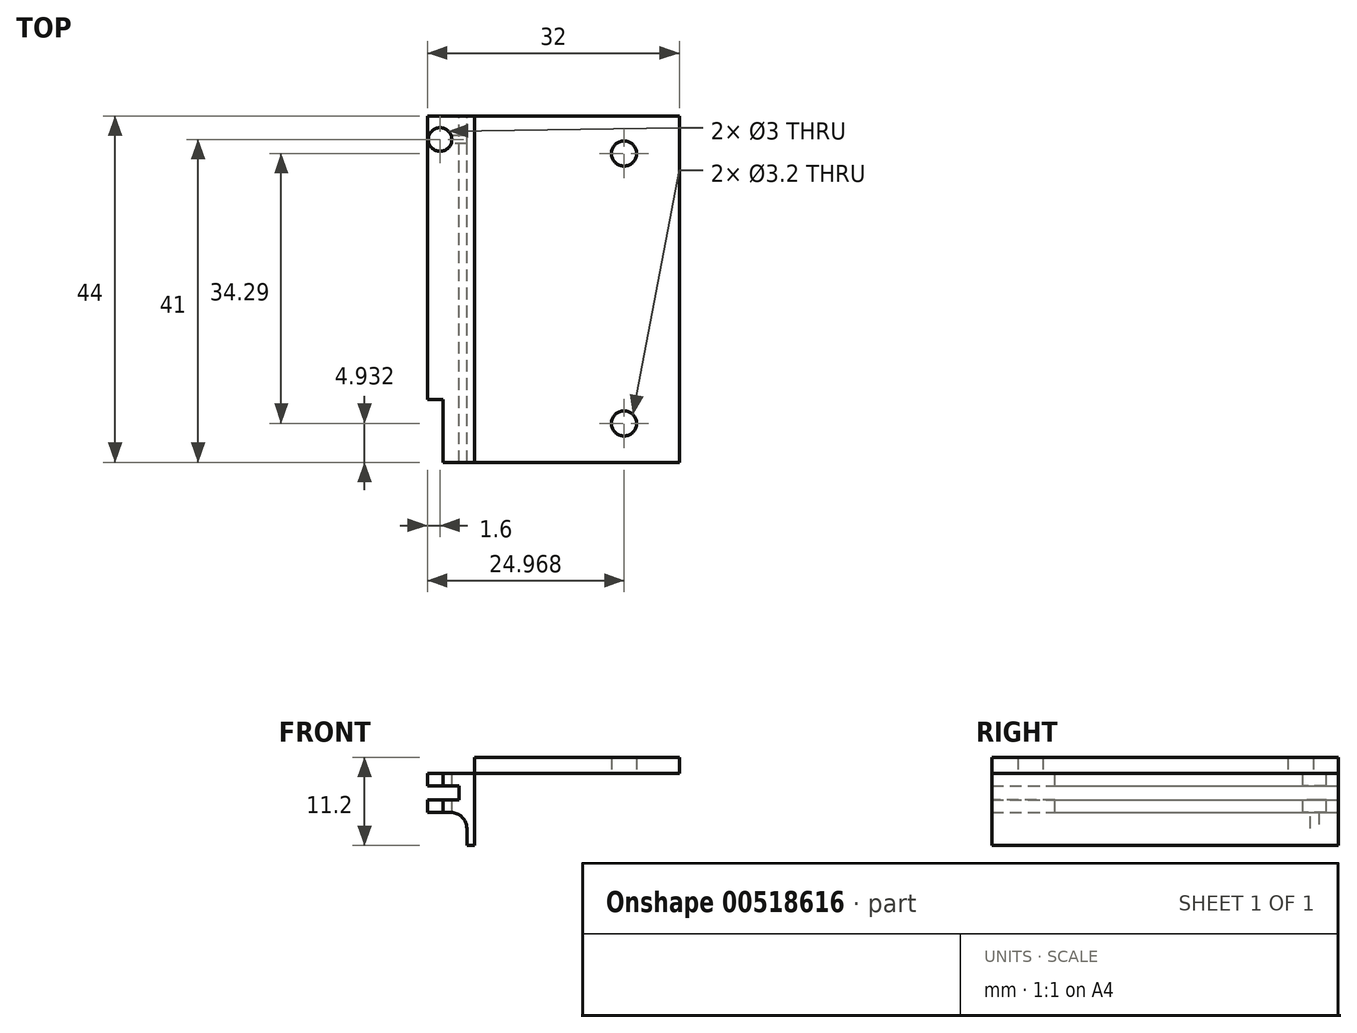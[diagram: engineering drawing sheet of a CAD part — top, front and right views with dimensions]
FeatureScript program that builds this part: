
annotation { "Feature Type Name" : "Feature", "Feature Type Description" : "" }
export const myFeature = defineFeature(function(context is Context, id is Id, definition is map)
    precondition{}
    {
        {
            var Q0;
            Q0=qCreatedBy(makeId("Front.planeOp"),FACE);
            var sketch = newSketch(context, id + "F0", { "sketchPlane" : qUnion([Q0])});
            skLineSegment(sketch, "E0", {"start": v(0, 0) * mm, "end": v(0, 9.2) * mm});
            skLineSegment(sketch, "E1", {"start": v(0, 9.2) * mm, "end": v(-6, 9.2) * mm});
            skLineSegment(sketch, "E2", {"start": v(-6, 9.2) * mm, "end": v(-6, 7.6) * mm});
            skLineSegment(sketch, "E3", {"start": v(-6, 7.6) * mm, "end": v(-2, 7.6) * mm});
            skLineSegment(sketch, "E4", {"start": v(-2, 7.6) * mm, "end": v(-2, 5.8) * mm});
            skLineSegment(sketch, "E5", {"start": v(-2, 5.8) * mm, "end": v(-6, 5.8) * mm});
            skLineSegment(sketch, "E6", {"start": v(-6, 5.8) * mm, "end": v(-6, 4.2) * mm});
            skLineSegment(sketch, "E7", {"start": v(-6, 4.2) * mm, "end": v(-1, 4.2) * mm});
            skLineSegment(sketch, "E8", {"start": v(-1, 4.2) * mm, "end": v(-1, 0) * mm});
            skLineSegment(sketch, "E9", {"start": v(-1, 0) * mm, "end": v(0, 0) * mm});
            skSolve(sketch);
        }
        {
            var Q0;
            Q0=makeQuery(id+"F0.imprint","IMPRINT",FACE,{"disambiguationData":[TD([[makeQuery(id+"F0.imprint","IMPRINT",EDGE,{"derivedFrom":sQuery(id+"F0.wireOp",EDGE,"E0")}),1.0]])]});
            extrude(context, id + "F1", {"entities" : qUnion([Q0]), "depth" : 44 * mm, "offsetDistance" : 25 * mm});
        }
        {
            var Q0;
            Q0=makeQuery(id+"F1.opExtrude","SWEPT_FACE",FACE,{"disambiguationData":[OSD([sQuery(id+"F0.wireOp",EDGE,"E1")])]});
            var sketch = newSketch(context, id + "F2", { "sketchPlane" : qUnion([Q0])});
            skCircle(sketch, "E10", {"center": v(-4.4, -3) * mm, "radius": 1.5 * mm});
            skSolve(sketch);
        }
        {
            var Q0;
            Q0=makeQuery(id+"F2.imprint","IMPRINT",FACE,{"disambiguationData":[TD([[makeQuery(id+"F2.imprint","IMPRINT",EDGE,{"derivedFrom":sQuery(id+"F2.wireOp",EDGE,"E10")}),1.0]])]});
            extrude(context, id + "F3", {"entities" : qUnion([Q0]), "operationType" : NewBodyOperationType.REMOVE, "endBound" : BoundingType.THROUGH_ALL, "oppositeDirection" : true, "depth" : 25 * mm, "offsetDistance" : 25 * mm});
        }
        {
            var Q0;
            Q0=makeQuery(id+"F1.opExtrude","SWEPT_FACE",FACE,{"disambiguationData":[OSD([sQuery(id+"F0.wireOp",EDGE,"E1")])]});
            var sketch = newSketch(context, id + "F4", { "sketchPlane" : qUnion([Q0])});
            skLineSegment(sketch, "E11.bottom", {"start": v(-6, -44) * mm, "end": v(-4, -44) * mm});
            skLineSegment(sketch, "E11.top", {"start": v(-6, -36) * mm, "end": v(-4, -36) * mm});
            skLineSegment(sketch, "E11.left", {"start": v(-6, -44) * mm, "end": v(-6, -36) * mm});
            skLineSegment(sketch, "E11.right", {"start": v(-4, -44) * mm, "end": v(-4, -36) * mm});
            skSolve(sketch);
        }
        {
            var Q0;
            Q0=makeQuery(id+"F4.imprint","IMPRINT",FACE,{"disambiguationData":[TD([[makeQuery(id+"F4.imprint","IMPRINT",EDGE,{"derivedFrom":sQuery(id+"F4.wireOp",EDGE,"E11.bottom")}),-1.0]])]});
            extrude(context, id + "F5", {"entities" : qUnion([Q0]), "operationType" : NewBodyOperationType.REMOVE, "endBound" : BoundingType.THROUGH_ALL, "oppositeDirection" : true, "depth" : 25 * mm, "offsetDistance" : 25 * mm});
        }
        {
            var Q0;
            Q0=makeQuery(id+"F1.opExtrude","SWEPT_EDGE",EDGE,{"disambiguationData":[OSD([sQuery(id+"F0.wireOp",EDGE,"E7"),sQuery(id+"F0.wireOp",EDGE,"E8")])]});
            fillet(context, id + "F6", {"entities" : qUnion([Q0]), "radius" : 2 * mm, "tangentPropagation" : true, "allowEdgeOverflow" : false});
        }
        {
            var Q0;
            Q0=makeQuery(id+"F1.opExtrude","SWEPT_FACE",FACE,{"disambiguationData":[OSD([sQuery(id+"F0.wireOp",EDGE,"E1")])]});
            var sketch = newSketch(context, id + "F7", { "sketchPlane" : qUnion([Q0])});
            skLineSegment(sketch, "E12.bottom", {"start": v(0, 0) * mm, "end": v(26, 0) * mm});
            skLineSegment(sketch, "E12.top", {"start": v(0, -44) * mm, "end": v(26, -44) * mm});
            skLineSegment(sketch, "E12.left", {"start": v(0, 0) * mm, "end": v(0, -44) * mm});
            skLineSegment(sketch, "E12.right", {"start": v(26, 0) * mm, "end": v(26, -44) * mm});
            skCircle(sketch, "E13", {"center": v(18.97, -4.78) * mm, "radius": 1.6 * mm});
            skCircle(sketch, "E14.0", {"center": v(-4.4, -3) * mm, "radius": 1.5 * mm});
            skCircle(sketch, "E15", {"center": v(18.97, -39.07) * mm, "radius": 1.6 * mm});
            skSolve(sketch);
        }
        {
            var Q0;
            Q0=makeQuery(id+"F7.imprint","IMPRINT",FACE,{"disambiguationData":[TD([[makeQuery(id+"F7.imprint","IMPRINT",EDGE,{"derivedFrom":sQuery(id+"F7.wireOp",EDGE,"E12.bottom")}),-1.0]])]});
            extrude(context, id + "F8", {"entities" : qUnion([Q0]), "depth" : 2 * mm, "offsetDistance" : 25 * mm});
        }
    });
